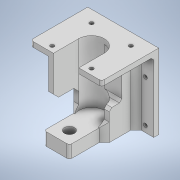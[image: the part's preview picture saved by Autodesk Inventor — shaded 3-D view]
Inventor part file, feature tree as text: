
AUTODESK INVENTOR PART (.ipt)
format: ipt  version: 2022 (Build 260153000, 153)  size: 373,248 bytes
history: native  units: mm
features: sketch x19, extrude x18, chamfer x5, hole x3, fillet x2, other x1
ambient origin geometry x8: Origin, YZ Plane, XZ Plane, XY Plane, X Axis, Y Axis, Z Axis, Center Point
bodies: Body1 (feature_tree)
feature tree (48):
  other  "Sólido1"
  sketch  "Esboço1"  dims[d0=56.0mm d1=10.0mm]
  extrude  "Extrusão1"  Depth=10.0mm
  extrude  "Extrusão2"  Depth=4.0mm TaperAngle=0.0deg
  hole  "Furo1"  [1 undecoded]
  hole  "Furo2"  [1 undecoded]
  extrude  "Extrusão3"  Depth=15.5mm
  extrude  "Extrusão4"  Depth=15.5mm
  sketch  "Esboço6"  dims[d25=25.0mm d26=39.0mm d27=0.0mm]
  extrude  "Extrusão5"  Depth=20.0mm
  extrude  "Extrusão6"  Depth=3.0mm
  extrude  "Extrusão7"  Depth=3.0mm
  extrude  "Extrusão8"  Depth=20.0mm TaperAngle=0.0deg
  extrude  "Extrusão9"  Depth=14.0mm TaperAngle=0.0deg
  extrude  "Extrusão10"  Depth=14.0mm TaperAngle=0.0deg
  chamfer  "Chanfro2"  Distance=39.0mm
  fillet  "Arredondamento1"  Radius=10.0mm
  hole  "Furo3"  [1 undecoded]
  extrude  "Extrusão11"  Depth=10.0mm TaperAngle=0.0deg
  fillet  "Arredondamento2"  Radius=2.0mm
  extrude  "Extrusão12"  Depth=4.0mm
  extrude  "Extrusão13"  Depth=4.0mm
  extrude  "Extrusão14"  Depth=14.0mm TaperAngle=0.0deg
  chamfer  "Chanfro3"  Distance=4.0mm Angle=45.0deg
  extrude  "Extrusão15"  TaperAngle=0.0deg  [1 undecoded]
  chamfer  "Chanfro4"  Distance=4.0mm Angle=45.0deg
  extrude  "Extrusão16"  Depth=2.0mm
  extrude  "Extrusão17"  Depth=4.0mm
  chamfer  "Chanfro5"  Distance=5.0mm
  extrude  "Extrusão18"  Depth=4.0mm
  chamfer  "Chanfro6"  Distance=2.0mm
  sketch  "Esboço2"  dims[d2=20.0mm d3=4.0mm d4=0.0mm]
  sketch  "Esboço3"  dims[d5=52.426mm d6=0.0mm]
  sketch  "Esboço4"  dims[d10=8.0mm d11=6.0mm d12=4.0mm d13=2.0mm d14=90.0deg d15=8.0mm d16=20.594885mm]
  sketch  "Esboço5"  dims[d17=3.0mm d18=6.0mm d19=4.0mm d20=2.0mm d21=90.0deg d22=8.0mm d23=20.594885mm d24=10.0mm]
  sketch  "Esboço7"  dims[d28=22.0mm d29=0.0mm d30=15.5mm]
  sketch  "Esboço8"  dims[d31=15.5mm d32=15.5mm]
  sketch  "Esboço9"  dims[d33=15.5mm d34=20.0mm]
  sketch  "Esboço10"  dims[d35=0.0mm d36=0.0mm d37=3.0mm]
  sketch  "Esboço11"  dims[d38=3.0mm d39=3.0mm]
  sketch  "Esboço12"  dims[d40=3.0mm d41=20.0mm d42=0.0mm]
  sketch  "Esboço13"  dims[d43=4.0mm d44=14.0mm d45=0.0mm]
  sketch  "Esboço14"  dims[d46=4.0mm d47=14.0mm d48=0.0mm d49=39.0mm d50=0.0mm d51=10.0mm d52=0.0mm]
  sketch  "Esboço15"  dims[d53=4.0mm d54=2.0mm d55=45.0deg d56=2.0mm]
  sketch  "Esboço16"  dims[d57=33.0mm]
  sketch  "Esboço17"  dims[d58=3.0mm d59=6.0mm d60=4.0mm d61=2.0mm d62=90.0deg d63=8.0mm d64=20.594885mm d65=10.0mm d66=0.0mm d67=2.0mm]
  sketch  "Esboço18"  dims[d68=0.0mm d69=0.0mm d70=4.0mm]
  sketch  "Esboço19"  dims[d71=14.0mm d72=0.0mm d73=4.0mm d74=14.0mm d75=0.0mm d76=4.0mm d77=2.0mm d78=45.0deg d79=0.0mm d80=0.0mm d81=4.0mm d82=2.0mm d83=45.0deg d84=2.5mm d85=4.0mm d86=5.0mm d87=2.5mm d88=4.0mm d89=5.0mm d90=2.0mm d91=0.0mm d92=2.5mm d93=4.0mm d94=5.0mm d95=2.5mm d96=4.0mm d97=5.0mm d98=2.0mm d99=0.0mm d100=2.0mm d101=2.0mm d102=45.0deg d103=15.5mm d104=15.5mm d105=14.0mm d106=2.0mm d107=0.0mm d108=2.0mm d109=2.0mm d110=45.0deg]
note: 4 required parameter values undecoded (feature->parameter linkage not recoverable at this tier; creation-order binding heuristic only, values carry confidence <= 0.55)
